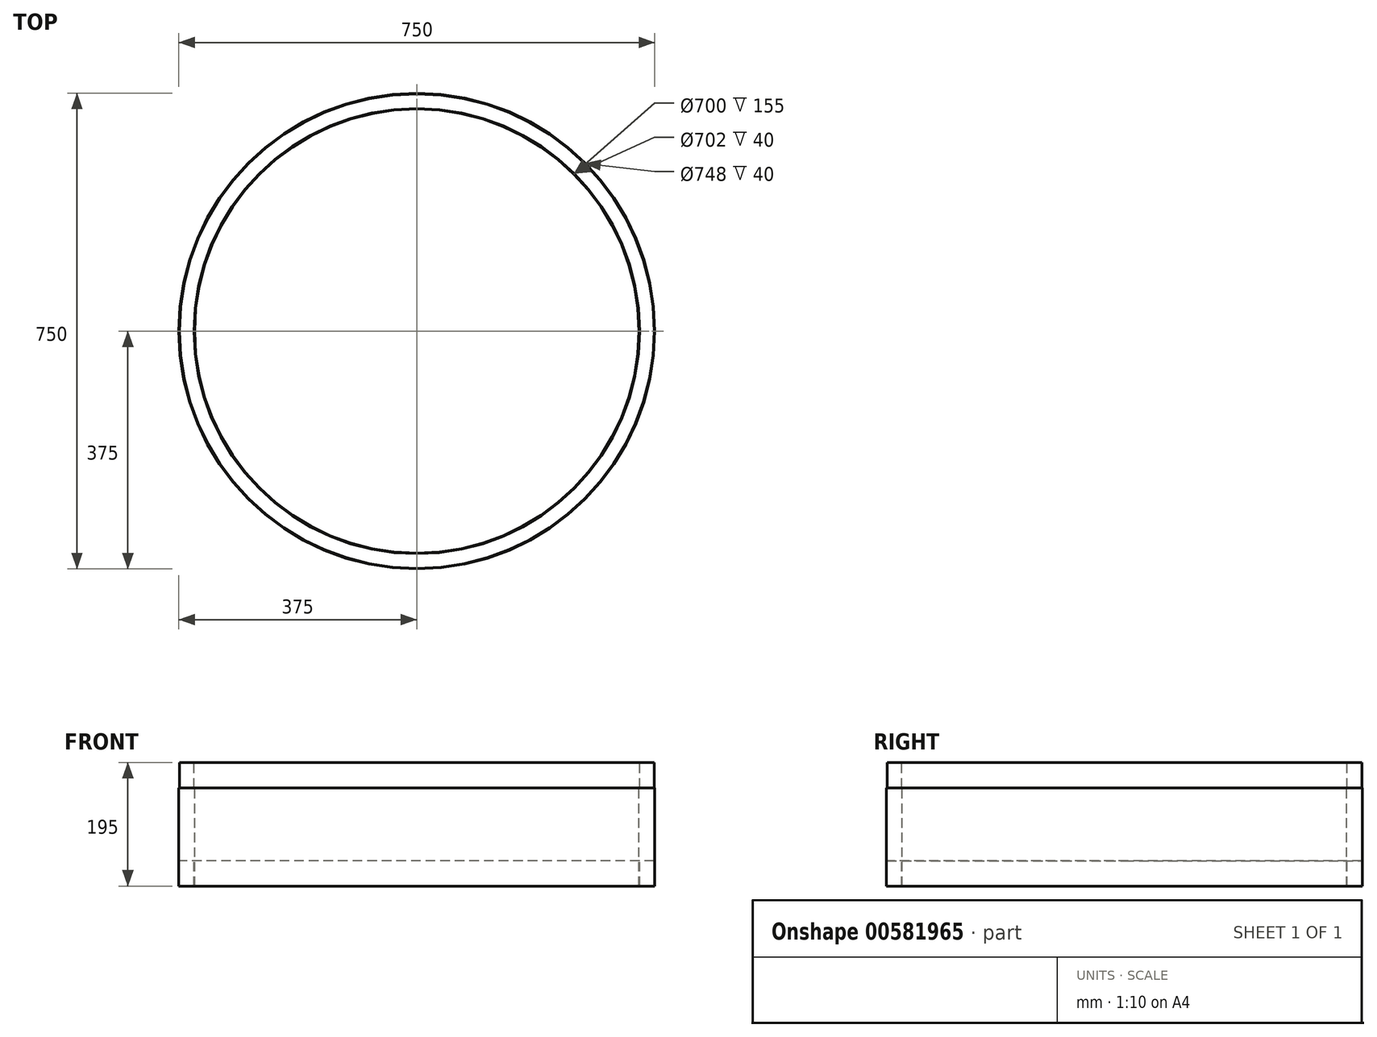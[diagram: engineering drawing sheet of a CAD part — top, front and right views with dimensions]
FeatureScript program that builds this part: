
annotation { "Feature Type Name" : "Feature", "Feature Type Description" : "" }
export const myFeature = defineFeature(function(context is Context, id is Id, definition is map)
    precondition{}
    {
        {
            var Q0;
            Q0=qCreatedBy(makeId("Front.planeOp"),FACE);
            var sketch = newSketch(context, id + "F0", { "sketchPlane" : qUnion([Q0])});
            skLineSegment(sketch, "E0", {"start": v(0, 345.75) * mm, "end": v(0, -558.03) * mm, "construction": true});
            skLineSegment(sketch, "E1", {"start": v(-350, -518.84) * mm, "end": v(-350, -363.84) * mm});
            skLineSegment(sketch, "E2", {"start": v(-350, -363.84) * mm, "end": v(-351, -363.84) * mm});
            skLineSegment(sketch, "E3", {"start": v(-351, -363.84) * mm, "end": v(-351, -323.84) * mm});
            skLineSegment(sketch, "E4", {"start": v(-351, -323.84) * mm, "end": v(-374, -323.84) * mm});
            skLineSegment(sketch, "E5", {"start": v(-374, -323.84) * mm, "end": v(-374, -363.84) * mm});
            skLineSegment(sketch, "E6", {"start": v(-374, -363.84) * mm, "end": v(-375, -363.84) * mm});
            skLineSegment(sketch, "E7", {"start": v(-375, -363.84) * mm, "end": v(-375, -518.84) * mm});
            skLineSegment(sketch, "E8", {"start": v(-375, -518.84) * mm, "end": v(-374, -518.84) * mm});
            skLineSegment(sketch, "E9", {"start": v(-374, -518.84) * mm, "end": v(-374, -478.84) * mm});
            skLineSegment(sketch, "E10", {"start": v(-374, -478.84) * mm, "end": v(-351, -478.84) * mm});
            skLineSegment(sketch, "E11", {"start": v(-351, -478.84) * mm, "end": v(-351, -518.84) * mm});
            skLineSegment(sketch, "E12", {"start": v(-351, -518.84) * mm, "end": v(-350, -518.84) * mm});
            skSolve(sketch);
        }
        {
            var Q0;
            Q0=qSketchRegion(id+"F0",true);
            var Q1;
            Q1=sQuery(id+"F0.wireOp",EDGE,"E0");
            revolve(context, id + "F1", {"entities" : qUnion([Q0]), "axis" : qUnion([Q1]), "revolveType" : RevolveType.FULL});
        }
    });
